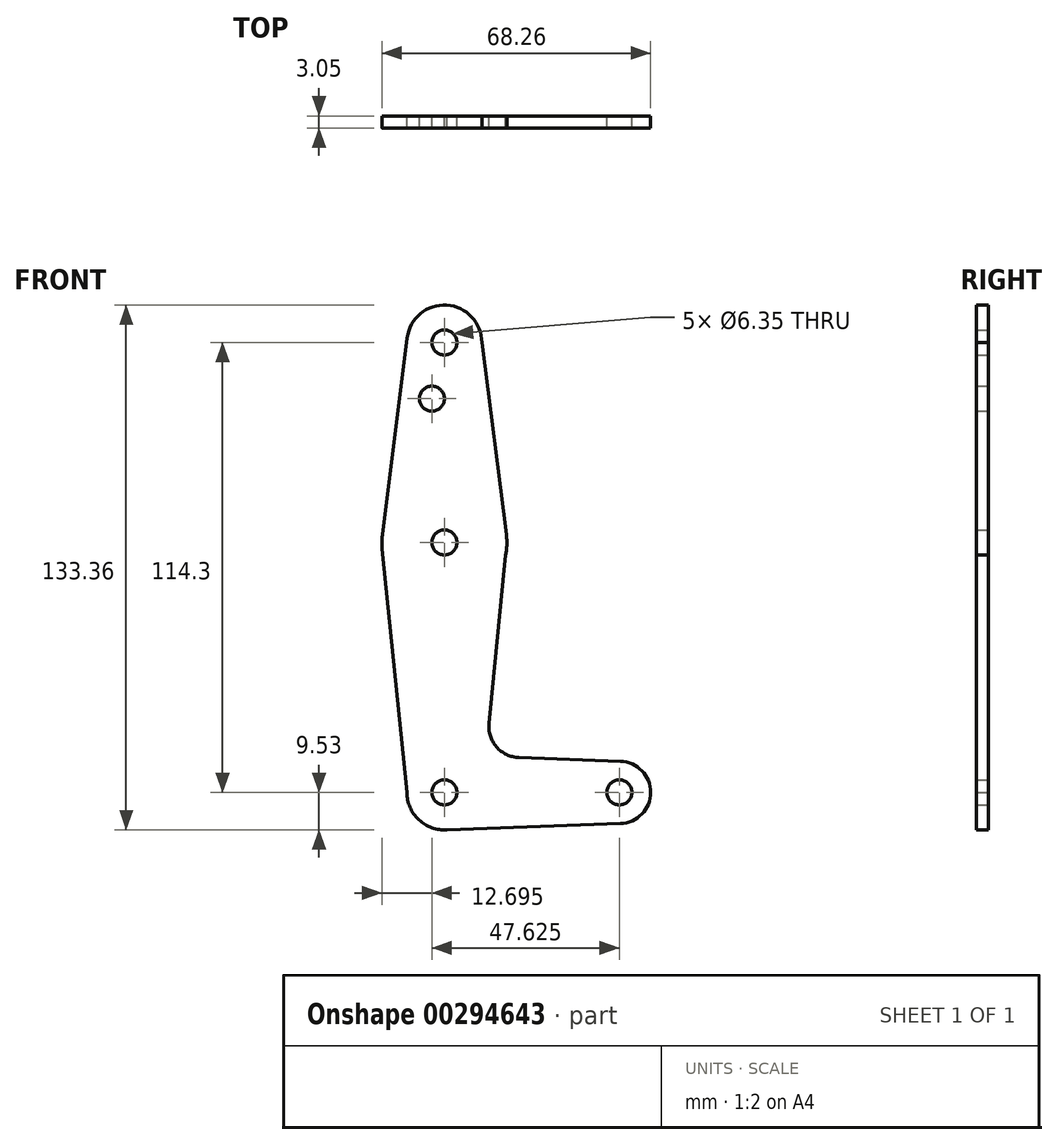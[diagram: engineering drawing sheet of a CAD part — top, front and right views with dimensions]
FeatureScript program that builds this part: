
annotation { "Feature Type Name" : "Feature", "Feature Type Description" : "" }
export const myFeature = defineFeature(function(context is Context, id is Id, definition is map)
    precondition{}
    {
        {
            var Q0;
            Q0=qCreatedBy(makeId("Front.planeOp"),FACE);
            var sketch = newSketch(context, id + "F0", { "sketchPlane" : qUnion([Q0])});
            skCircle(sketch, "E0", {"center": v(0, 0) * mm, "radius": 9.53 * mm});
            skCircle(sketch, "E1", {"center": v(44.45, 0) * mm, "radius": 7.94 * mm});
            skCircle(sketch, "E2", {"center": v(0, 63.5) * mm, "radius": 15.88 * mm});
            skCircle(sketch, "E3", {"center": v(0, 114.3) * mm, "radius": 9.53 * mm});
            skLineSegment(sketch, "E4", {"start": v(0, 114.3) * mm, "end": v(0, 63.5) * mm, "construction": true});
            skLineSegment(sketch, "E5", {"start": v(0, 63.5) * mm, "end": v(0, 0) * mm, "construction": true});
            skLineSegment(sketch, "E6", {"start": v(44.45, 0) * mm, "end": v(0, 0) * mm, "construction": true});
            skLineSegment(sketch, "E7", {"start": v(15.88, 63.5) * mm, "end": v(11.32, 17.58) * mm});
            skLineSegment(sketch, "E8", {"start": v(18.95, 8.85) * mm, "end": v(44.73, 7.93) * mm});
            skLineSegment(sketch, "E9", {"start": v(0, -9.53) * mm, "end": v(44.73, -7.93) * mm});
            skLineSegment(sketch, "E10", {"start": v(-9.52, 0) * mm, "end": v(-15.8, 61.9) * mm});
            skLineSegment(sketch, "E11", {"start": v(-9.45, 115.5) * mm, "end": v(-15.75, 65.48) * mm});
            skLineSegment(sketch, "E12", {"start": v(9.52, 114.3) * mm, "end": v(15.75, 65.5) * mm});
            skCircle(sketch, "E13", {"center": v(0, 114.3) * mm, "radius": 3.18 * mm});
            skCircle(sketch, "E14", {"center": v(-3.17, 100.03) * mm, "radius": 3.18 * mm});
            skCircle(sketch, "E15", {"center": v(0, 63.5) * mm, "radius": 3.18 * mm});
            skCircle(sketch, "E16", {"center": v(0, 0) * mm, "radius": 3.18 * mm});
            skCircle(sketch, "E17", {"center": v(44.45, 0) * mm, "radius": 3.18 * mm});
            skPoint(sketch, "E18.newPointB", {"position": v(9.57, 0) * mm});
            skArc(sketch, "E18.filletArc", {"start": v(11.32, 17.58) * mm, "mid": v(13.24, 11.56) * mm, "end": v(18.95, 8.85) * mm});
            skSolve(sketch);
        }
        {
            var Q0;
            Q0 = qSketchRegion(id + "F0", true);
            extrude(context, id + "F1", {"entities" : qUnion([Q0]), "depth" : 3.05 * mm});
        }
    });
